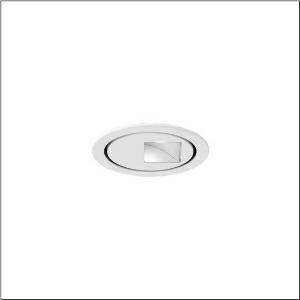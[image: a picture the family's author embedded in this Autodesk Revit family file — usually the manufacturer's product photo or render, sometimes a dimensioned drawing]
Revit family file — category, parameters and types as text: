
# Revit family: lunis_11_micro_round_51dj11cd1wn21
name_source: partatom
category: Lighting Fixtures
units: mm (PartAtom-declared; Revit-internal decimal feet)

## family parameters
Cut with Voids When Loaded = No
Host = Face
Light Source = No
Part Type = Normal
Room Calculation Point = No
Round Connector Dimension = Use Diameter
Shared = No

## types (1)
- Lunis 11 micro round (1 x LED 4000K / CRI = 90 (unbekannt), 1210 lm, 4000K)
    Apparent Load = 20 VA
    CIE Flux Codes = 42 75 96 100 100
    Color Rendering = 90
    Color Temperature = 4000K
    Default Elevation = 1800 mm
    Description = Lunis 11 micro round, downlight, light control with wallwasher, of highly reflective aluminium, highly specular, light emission: direct distribution, LED rated luminous flux: 1.210lm, light colour: 940, control gear: ECG, with terminal, 5-pole, mains connection: 220..230V, AC/DC, 0/50..60Hz, LED module, luminaire module, of aluminium, highly specular, white, diameter: 114mm, clamping range: 1..40mm, recessing ring, of plastic, traffic white (RAL 9016), protection rating (complete): IP20, insulation class (complete): insulation class II (safety insulation), certification: CE, permissible ambient temperature for indoor applications: 0..+35°C, packaging unit: 1 piece
    Height = 0 mm  [stored 0 ft]
    Lamp = 1 x LED 4000K / CRI >= 90 (unbekannt)
    Lamp Light Flux = 1210 lm
    Lamp count = 1
    Length = 114 mm
    Luminous efficacy = 61 lm/W
    Manufacturer = Siteco
    ModVariant = No
    Model = 51DJ11CD1WN21
    Mounting Place = Ceiling
    Mounting Type = Recessed
    Number of Poles = 1
    OnlyDefault = Yes
    Power Factor = 1
    Product Name = Lunis 11 micro round
    Product group = downlight | ceiling recessed
    ProductGroupID = 402
    Protection Class = Protection class II
    Protection Degree = IP 20
    RLX_Detail_Level = 1
    RlxData = <blob elided: 40885 chars, md5=a72f31ab>
    Socket = socket
    Standby Power = 0 W
    System Light Flux = 1210 lm
    System Power = 20 W
    Type Comments = Product without accessories
    Type Image = l_1004773.jpg
    URL = http://relux.com
    VarID = ---
    Voltage = 0 V
    Weight = 0.00 kg
    Width = 114 mm

note: [stored X ft] marks values corroborated as IEEE doubles in the binary element streams (Revit-internal decimal feet)

## geometry (parser evidence)
native form markers: Blend x4, Sweep x11
no freeform markers — native parametric forms only
